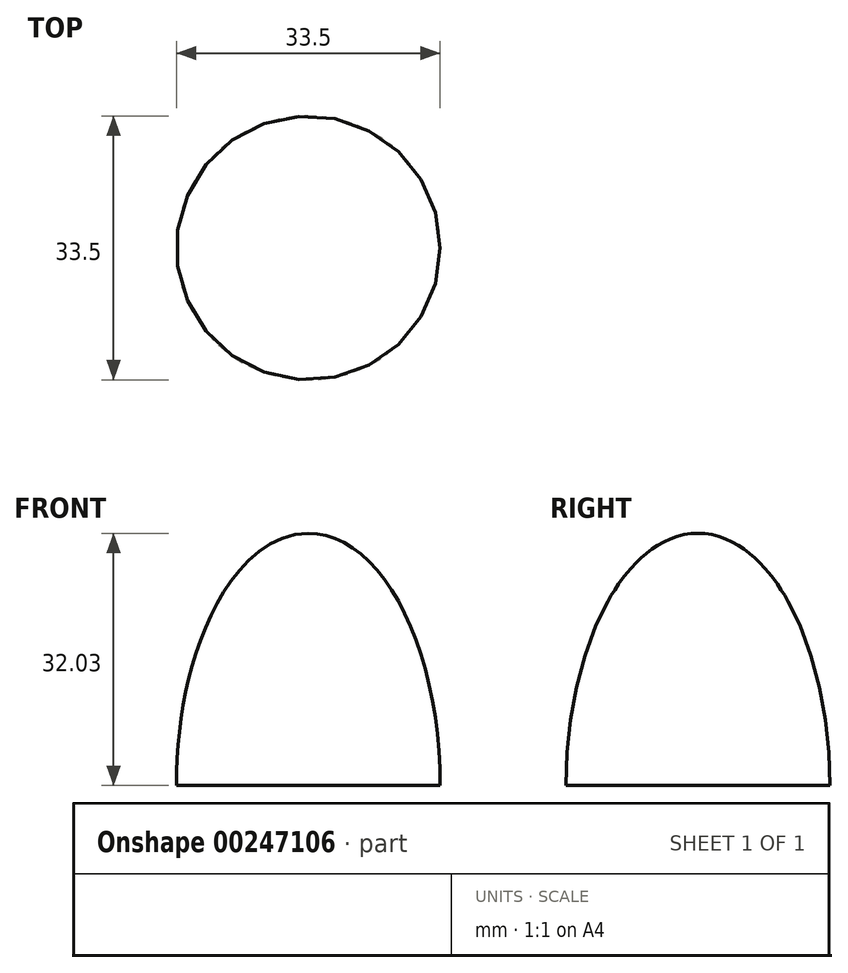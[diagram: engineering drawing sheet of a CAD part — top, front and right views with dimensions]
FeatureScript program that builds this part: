
annotation { "Feature Type Name" : "Feature", "Feature Type Description" : "" }
export const myFeature = defineFeature(function(context is Context, id is Id, definition is map)
    precondition{}
    {
        {
            var Q0;
            Q0=qCreatedBy(makeId("Front.planeOp"),FACE);
            var sketch = newSketch(context, id + "F0", { "sketchPlane" : qUnion([Q0])});
            skEllipticalArc(sketch, "E0", {});
            skLineSegment(sketch, "E1", {"start": v(0, 0) * mm, "end": v(16.75, 0) * mm});
            skLineSegment(sketch, "E2", {"start": v(0, 0) * mm, "end": v(0, 32.03) * mm});
            skPoint(sketch, "E3.orphan", {"position": v(-16.75, 0) * mm});
            const initialGuessF0  = {"E0": [0, 0, 0, 1, 0.03203380107879639, 0.016752921665044586, 4.71238898038469, 0]};
            skSetInitialGuess(sketch, initialGuessF0);
            skSolve(sketch);
        }
        {
            var Q0;
            Q0 = qSketchRegion(id + "F0", true);
            var Q1;
            Q1=sQuery(id+"F0.wireOp",EDGE,"E2");
            revolve(context, id + "F1", {"entities" : qUnion([Q0]), "axis" : qUnion([Q1]), "revolveType" : RevolveType.FULL});
        }
    });
